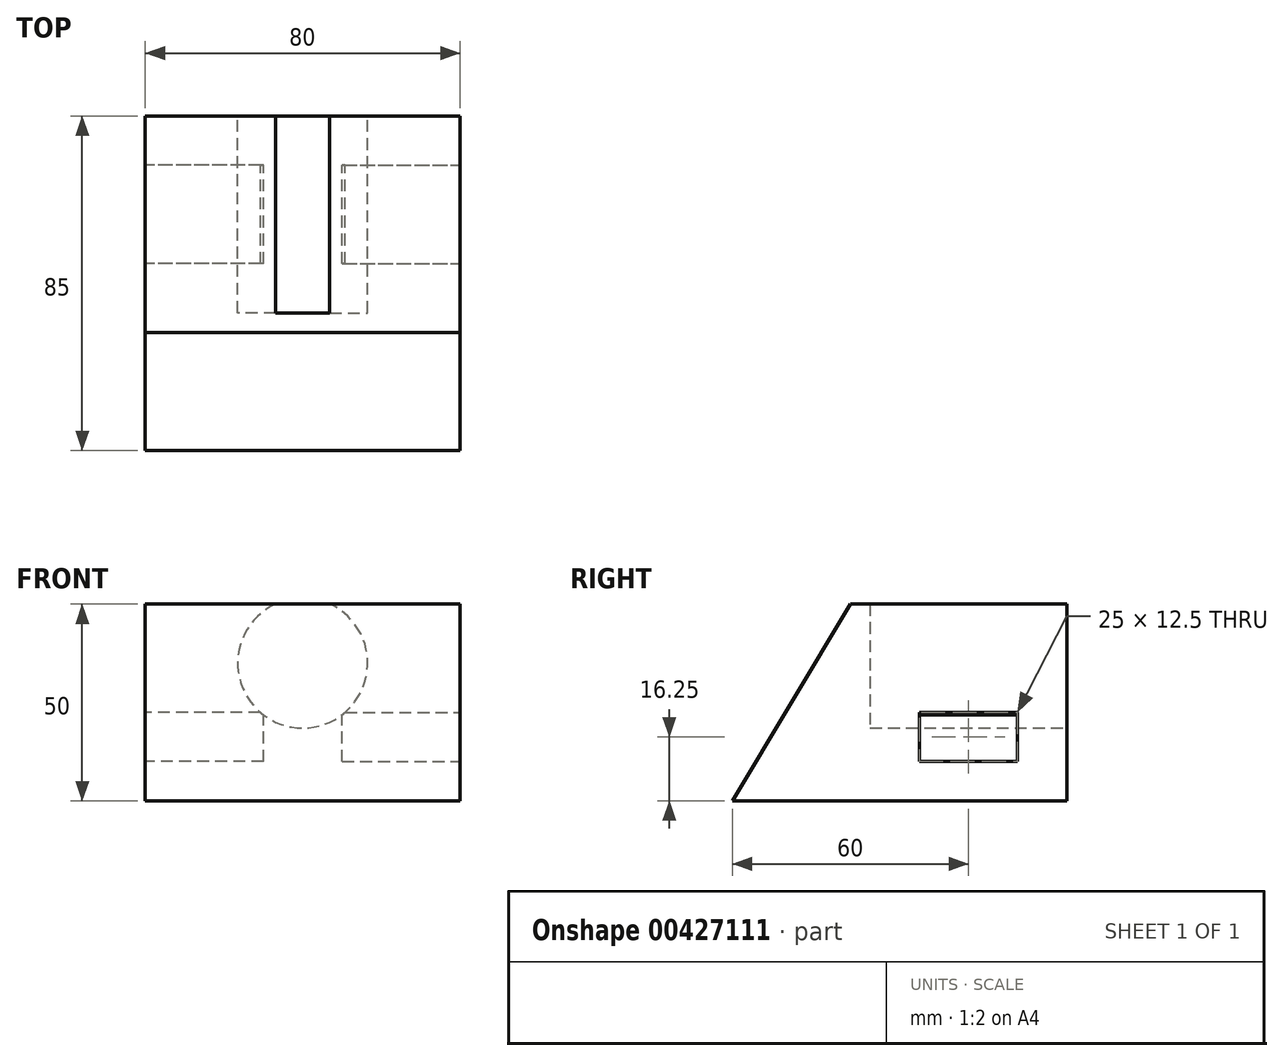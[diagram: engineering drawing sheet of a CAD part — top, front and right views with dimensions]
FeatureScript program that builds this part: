
annotation { "Feature Type Name" : "Feature", "Feature Type Description" : "" }
export const myFeature = defineFeature(function(context is Context, id is Id, definition is map)
    precondition{}
    {
        {
            var Q0;
            Q0=qCreatedBy(makeId("Front.planeOp"),FACE);
            var sketch = newSketch(context, id + "F0", { "sketchPlane" : qUnion([Q0])});
            skLineSegment(sketch, "E0.bottom", {"start": v(0, 0) * mm, "end": v(80, 0) * mm});
            skLineSegment(sketch, "E0.top", {"start": v(0, 50) * mm, "end": v(80, 50) * mm});
            skLineSegment(sketch, "E0.left", {"start": v(0, 0) * mm, "end": v(0, 50) * mm});
            skLineSegment(sketch, "E0.right", {"start": v(80, 0) * mm, "end": v(80, 50) * mm});
            skLineSegment(sketch, "E1.bottom", {"start": v(0, 0) * mm, "end": v(100, 0) * mm, "construction": true});
            skLineSegment(sketch, "E1.top", {"start": v(0, 100) * mm, "end": v(100, 100) * mm, "construction": true});
            skLineSegment(sketch, "E1.left", {"start": v(0, 0) * mm, "end": v(0, 100) * mm, "construction": true});
            skLineSegment(sketch, "E1.right", {"start": v(100, 0) * mm, "end": v(100, 100) * mm, "construction": true});
            skSolve(sketch);
        }
        {
            var Q0;
            Q0 = qSketchRegion(id + "F0", true);
            extrude(context, id + "F1", {"entities" : qUnion([Q0]), "oppositeDirection" : true, "depth" : 85 * mm});
        }
        {
            var Q0;
            Q0=qCreatedBy(makeId("Right.planeOp"),FACE);
            var sketch = newSketch(context, id + "F2", { "sketchPlane" : qUnion([Q0])});
            skLineSegment(sketch, "E2", {"start": v(0, 0) * mm, "end": v(0, 30) * mm});
            skLineSegment(sketch, "E3", {"start": v(0, 0) * mm, "end": v(55, 0) * mm, "construction": true});
            skLineSegment(sketch, "E4", {"start": v(55, 0) * mm, "end": v(55, 10) * mm, "construction": true});
            skLineSegment(sketch, "E5.bottom", {"start": v(0, 0) * mm, "end": v(100, 0) * mm, "construction": true});
            skLineSegment(sketch, "E5.top", {"start": v(0, 100) * mm, "end": v(100, 100) * mm, "construction": true});
            skLineSegment(sketch, "E5.left", {"start": v(0, 0) * mm, "end": v(0, 100) * mm, "construction": true});
            skLineSegment(sketch, "E5.right", {"start": v(100, 0) * mm, "end": v(100, 100) * mm, "construction": true});
            skLineSegment(sketch, "E6", {"start": v(55, 10) * mm, "end": v(72.5, 10) * mm});
            skLineSegment(sketch, "E7", {"start": v(72.5, 10) * mm, "end": v(72.5, 22.5) * mm});
            skLineSegment(sketch, "E8", {"start": v(72.5, 22.5) * mm, "end": v(47.5, 22.5) * mm});
            skLineSegment(sketch, "E9", {"start": v(47.5, 22.5) * mm, "end": v(47.5, 10) * mm});
            skLineSegment(sketch, "E10", {"start": v(47.5, 10) * mm, "end": v(55, 10) * mm});
            skLineSegment(sketch, "E11", {"start": v(0, 0) * mm, "end": v(0, 50) * mm});
            skLineSegment(sketch, "E12", {"start": v(0, 50) * mm, "end": v(30, 50) * mm});
            skLineSegment(sketch, "E13", {"start": v(30, 50) * mm, "end": v(0, 0) * mm});
            skLineSegment(sketch, "E14", {"start": v(55, 0) * mm, "end": v(55, 35) * mm, "construction": true});
            skLineSegment(sketch, "E15", {"start": v(55, 35) * mm, "end": v(47.5, 35) * mm});
            skLineSegment(sketch, "E16", {"start": v(47.5, 47.5) * mm, "end": v(72.5, 47.5) * mm});
            skLineSegment(sketch, "E17", {"start": v(72.5, 35) * mm, "end": v(55, 35) * mm});
            skLineSegment(sketch, "E18", {"start": v(47.5, 35) * mm, "end": v(47.5, 47.5) * mm});
            skLineSegment(sketch, "E19", {"start": v(72.5, 47.5) * mm, "end": v(72.5, 35) * mm});
            skSolve(sketch);
        }
        {
            var Q0;
            Q0=makeQuery(id+"F2.imprint","IMPRINT",FACE,{"disambiguationData":[TD([[makeQuery(id+"F2.imprint","IMPRINT",EDGE,{"derivedFrom":sQuery(id+"F2.wireOp",EDGE,"E6")}),1.0]])]});
            extrude(context, id + "F3", {"entities" : qUnion([Q0]), "operationType" : NewBodyOperationType.REMOVE, "depth" : 30 * mm});
        }
        {
            var Q0;
            Q0=makeQuery(id+"F1.opExtrude","SWEPT_FACE",FACE,{"disambiguationData":[OSD([sQuery(id+"F0.wireOp",EDGE,"E0.right")])]});
            cPlane(context, id + "F4", {"entities" : qUnion([Q0]), "cplaneType" : CPlaneType.OFFSET, "offset" : 0 * mm, "width" : 150 * mm, "height" : 150 * mm});
        }
        {
            var Q0;
            Q0=qCreatedBy(id+"F4.planeOp",FACE);
            var sketch = newSketch(context, id + "F5", { "sketchPlane" : qUnion([Q0])});
            skLineSegment(sketch, "E20", {"start": v(0, 0) * mm, "end": v(47.5, 0) * mm, "construction": true});
            skLineSegment(sketch, "E21", {"start": v(47.5, 0) * mm, "end": v(47.5, 10) * mm, "construction": true});
            skLineSegment(sketch, "E22.bottom", {"start": v(47.5, 10) * mm, "end": v(72.5, 10) * mm});
            skLineSegment(sketch, "E22.top", {"start": v(47.5, 22.5) * mm, "end": v(72.5, 22.5) * mm});
            skLineSegment(sketch, "E22.left", {"start": v(47.5, 10) * mm, "end": v(47.5, 22.5) * mm});
            skLineSegment(sketch, "E22.right", {"start": v(72.5, 10) * mm, "end": v(72.5, 22.5) * mm});
            skSolve(sketch);
        }
        {
            var Q0;
            Q0=makeQuery(id+"F5.imprint","IMPRINT",FACE,{"disambiguationData":[TD([[makeQuery(id+"F5.imprint","IMPRINT",EDGE,{"derivedFrom":sQuery(id+"F5.wireOp",EDGE,"E22.bottom")}),1.0]])]});
            extrude(context, id + "F6", {"entities" : qUnion([Q0]), "operationType" : NewBodyOperationType.REMOVE, "oppositeDirection" : true, "depth" : 30 * mm});
        }
        {
            var Q0;
            {var subQ2=sQuery(id+"F2.wireOp",EDGE,"E12");Q0=makeQuery(id+"F2.imprint","IMPRINT",FACE,{"disambiguationData":[TD([[makeQuery(id+"F2.imprint","IMPRINT",EDGE,{"derivedFrom":subQ2}),-1.0]])]});}
            extrude(context, id + "F7", {"entities" : qUnion([Q0]), "operationType" : NewBodyOperationType.REMOVE, "depth" : 80 * mm});
        }
        {
            var Q0;
            Q0=makeQuery(id+"F1.opExtrude","CAP_FACE",FACE,{"disambiguationData":[OSD([sQuery(id+"F0.wireOp",EDGE,"E0.bottom"),sQuery(id+"F0.wireOp",EDGE,"E0.top"),sQuery(id+"F0.wireOp",EDGE,"E0.left"),sQuery(id+"F0.wireOp",EDGE,"E0.right")])],"isStart":false});
            var sketch = newSketch(context, id + "F8", { "sketchPlane" : qUnion([Q0])});
            skLineSegment(sketch, "E23", {"start": v(0, 0) * mm, "end": v(-40, 0) * mm});
            skLineSegment(sketch, "E24", {"start": v(-40, 0) * mm, "end": v(-40, 35) * mm});
            skCircle(sketch, "E25", {"center": v(-40, 35) * mm, "radius": 16.5 * mm});
            skSolve(sketch);
        }
        {
            var Q0;
            {var subQ0=sQuery(id+"F8.wireOp",EDGE,"E25");var subQ1=makeQuery(id+"F8.imprint","INTERSECT",VERTEX,{"derivedFrom":[sQuery(id+"F8.wireOp",EDGE,"E24"),subQ0]});Q0=makeQuery(id+"F8.imprint","IMPRINT",FACE,{"disambiguationData":[TD([[makeQuery(id+"F8.imprint","IMPRINT",EDGE,{"disambiguationData":[TD([[subQ1,1.0]])],"derivedFrom":subQ0}),1.0]])]});}
            extrude(context, id + "F9", {"entities" : qUnion([Q0]), "operationType" : NewBodyOperationType.REMOVE, "oppositeDirection" : true, "depth" : 50 * mm});
        }
    });
